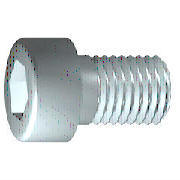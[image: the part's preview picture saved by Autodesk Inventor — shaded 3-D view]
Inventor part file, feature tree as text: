
AUTODESK INVENTOR PART (.ipt)
format: ipt  version: 2022 (Build 260153000, 153)  size: 192,000 bytes
history: native  units: mm (DEFAULTED — no unit token found)
features: sketch x2, other x1, extrude x1, plane x1, fillet x1
ambient origin geometry x7: Origin, YZ Plane, XY Plane, X Axis, Y Axis, Z Axis, Center Point
bodies: Solid1 (feature_tree)
feature tree (6):
  other  "Базовый элемент"
  extrude  "Паз"  Depth=17.9mm
  plane  "Work Plane1"
  fillet  "Fillet2"  Radius=0.429515mm
  sketch  "Эскиз1"
  sketch  "Эскиз2"
